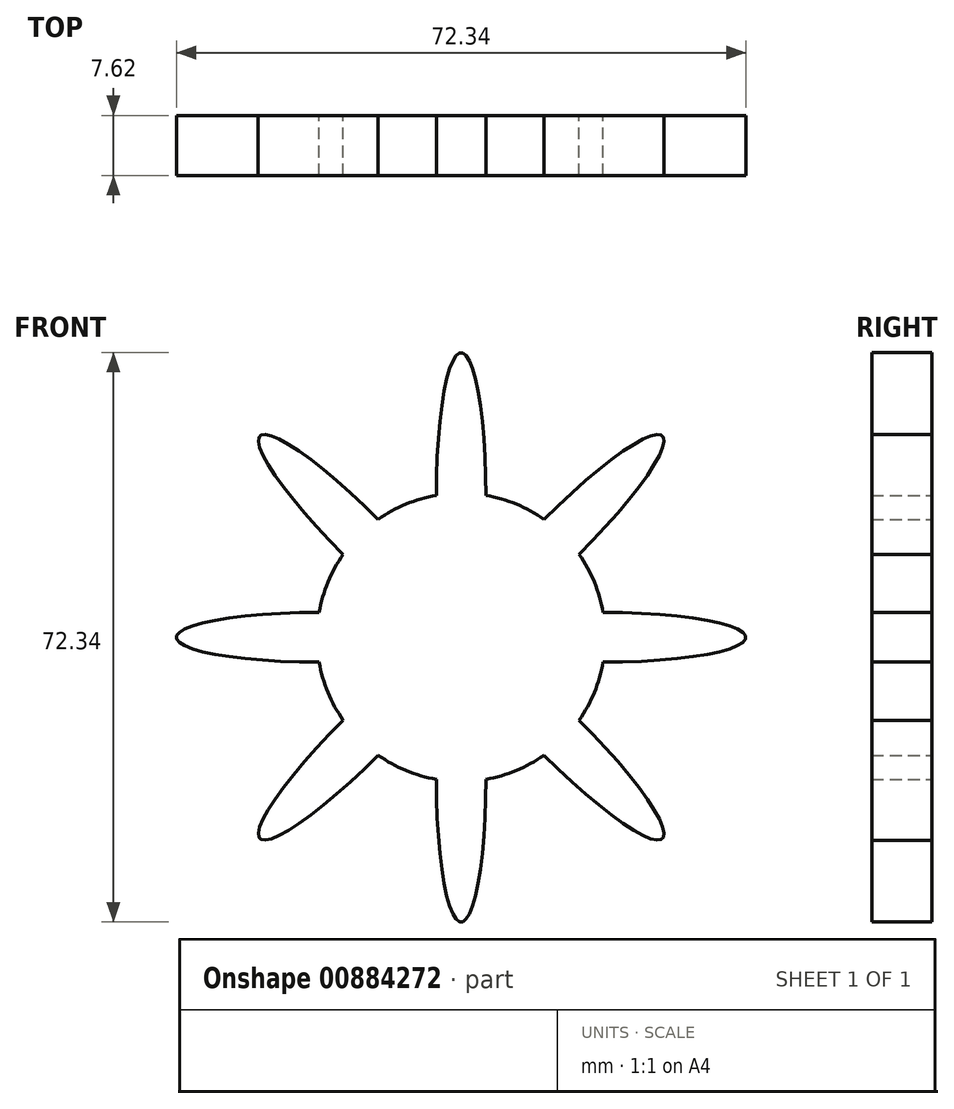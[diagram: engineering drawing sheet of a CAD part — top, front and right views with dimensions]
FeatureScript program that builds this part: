
annotation { "Feature Type Name" : "Feature", "Feature Type Description" : "" }
export const myFeature = defineFeature(function(context is Context, id is Id, definition is map)
    precondition{}
    {
        {
            var Q0;
            Q0=qCreatedBy(makeId("Front.planeOp"),FACE);
            var sketch = newSketch(context, id + "F0", { "sketchPlane" : qUnion([Q0])});
            skArc(sketch, "E0", {"start": v(-3.15, 18.04) * mm, "mid": v(-7, 16.92) * mm, "end": v(-10.53, 14.98) * mm});
            skEllipticalArc(sketch, "E1", {});
            skEllipticalArc(sketch, "E2.1.0", {});
            skEllipticalArc(sketch, "E2.2.0", {});
            skEllipticalArc(sketch, "E2.3.0", {});
            skEllipticalArc(sketch, "E2.4.0", {});
            skEllipticalArc(sketch, "E2.5.0", {});
            skEllipticalArc(sketch, "E2.6.0", {});
            skEllipticalArc(sketch, "E2.7.0", {});
            skArc(sketch, "E3.trimOffspring", {"start": v(-14.98, 10.53) * mm, "mid": v(-16.92, 7) * mm, "end": v(-18.04, 3.15) * mm});
            skArc(sketch, "E4.trimOffspring", {"start": v(10.53, 14.98) * mm, "mid": v(7, 16.92) * mm, "end": v(3.15, 18.04) * mm});
            skArc(sketch, "E5.trimOffspring", {"start": v(18.04, 3.15) * mm, "mid": v(16.92, 7) * mm, "end": v(14.98, 10.53) * mm});
            skArc(sketch, "E6.trimOffspring", {"start": v(-18.04, -3.15) * mm, "mid": v(-16.92, -7) * mm, "end": v(-14.98, -10.53) * mm});
            skArc(sketch, "E7.trimOffspring", {"start": v(14.98, -10.53) * mm, "mid": v(16.92, -7) * mm, "end": v(18.04, -3.15) * mm});
            skArc(sketch, "E8.trimOffspring", {"start": v(3.15, -18.04) * mm, "mid": v(7, -16.92) * mm, "end": v(10.53, -14.98) * mm});
            skArc(sketch, "E9.trimOffspring", {"start": v(-10.53, -14.98) * mm, "mid": v(-7, -16.92) * mm, "end": v(-3.15, -18.04) * mm});
            const initialGuessF0  = {"E1": [0, 0.018313187600717998, 0, 1, 0.017857697366132283, 0.0031487543982639263, 4.697119685694693, 1.5860656214848936], "E2.1.0": [-0.012949379137609095, 0.012949379137609098, -0.7071067811865475, 0.7071067811865476, 0.017857697366132283, 0.0031487543982639263, 4.697119685694693, 1.5860656214848936], "E2.2.0": [-0.018313187600717998, 0, -1, 0, 0.017857697366132283, 0.0031487543982639263, 4.697119685694693, 1.5860656214848936], "E2.3.0": [-0.012949379137609098, -0.012949379137609095, -0.7071067811865476, -0.7071067811865475, 0.017857697366132283, 0.0031487543982639263, 4.697119685694693, 1.5860656214848936], "E2.4.0": [0, -0.018313187600717998, 0, -1, 0.017857697366132283, 0.0031487543982639263, 4.697119685694693, 1.5860656214848936], "E2.5.0": [0.012949379137609095, -0.0129493791376091, 0.7071067811865475, -0.7071067811865477, 0.017857697366132283, 0.0031487543982639263, 4.697119685694693, 1.5860656214848936], "E2.6.0": [0.018313187600717998, 0, 1, 0, 0.017857697366132283, 0.0031487543982639263, 4.697119685694693, 1.5860656214848936], "E2.7.0": [0.0129493791376091, 0.012949379137609093, 0.7071067811865477, 0.7071067811865474, 0.017857697366132283, 0.0031487543982639263, 4.697119685694693, 1.5860656214848936]};
            skSetInitialGuess(sketch, initialGuessF0);
            skSolve(sketch);
        }
        {
            var Q0;
            Q0=makeQuery(id+"F0.imprint","IMPRINT",FACE,{"disambiguationData":[TD([[makeQuery(id+"F0.imprint","IMPRINT",EDGE,{"derivedFrom":sQuery(id+"F0.wireOp",EDGE,"E0")}),1.0]])]});
            extrude(context, id + "F1", {"entities" : qUnion([Q0]), "depth" : 7.62 * mm, "offsetDistance" : 25.4 * mm});
        }
    });
